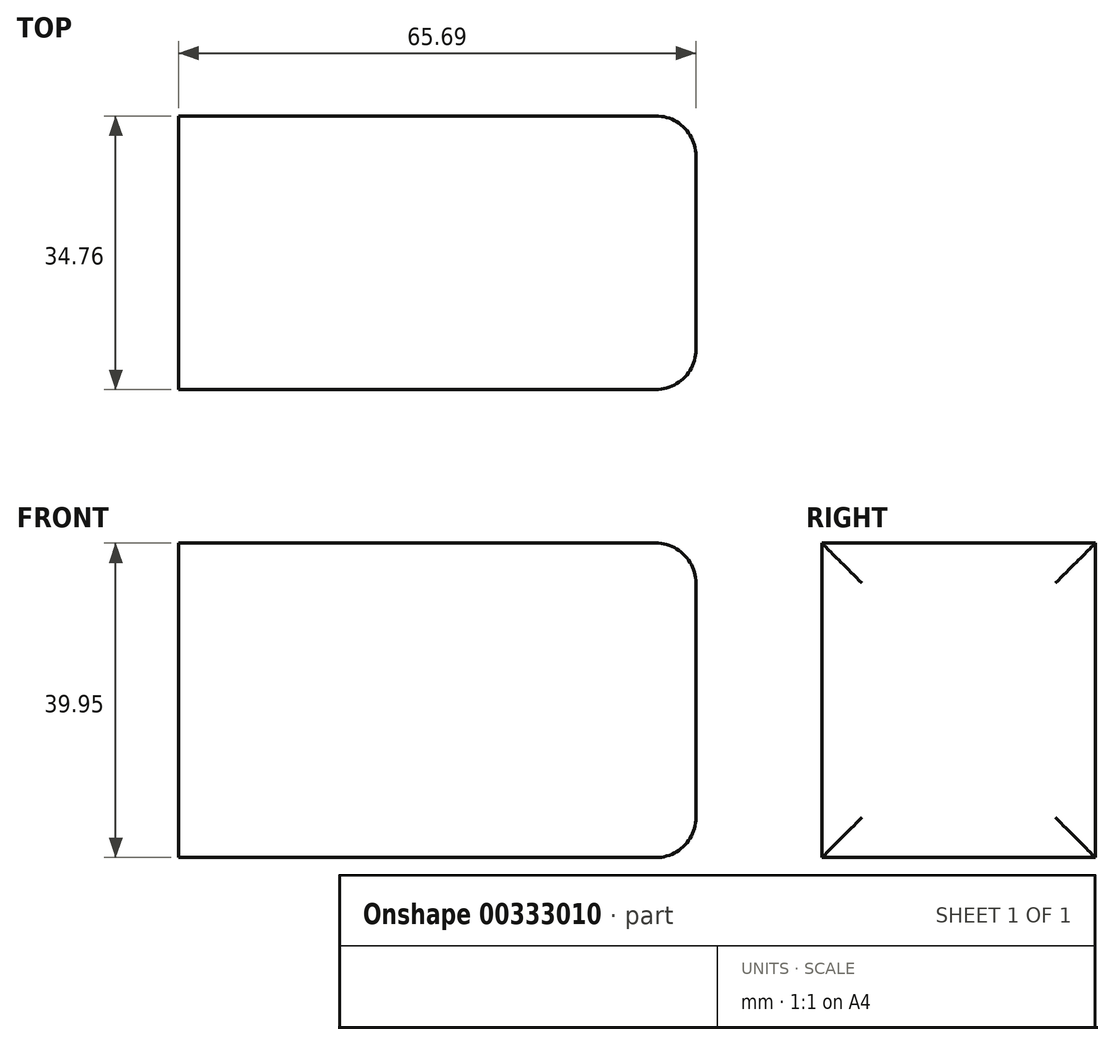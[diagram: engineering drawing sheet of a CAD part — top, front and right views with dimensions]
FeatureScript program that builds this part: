
annotation { "Feature Type Name" : "Feature", "Feature Type Description" : "" }
export const myFeature = defineFeature(function(context is Context, id is Id, definition is map)
    precondition{}
    {
        {
            var Q0;
            Q0=qCreatedBy(makeId("Top.planeOp"),FACE);
            var sketch = newSketch(context, id + "F0", { "sketchPlane" : qUnion([Q0])});
            skLineSegment(sketch, "E0.bottom", {"start": v(35.56, 34.76) * mm, "end": v(-30.13, 34.76) * mm});
            skLineSegment(sketch, "E0.top", {"start": v(35.56, 0) * mm, "end": v(-30.13, 0) * mm});
            skLineSegment(sketch, "E0.left", {"start": v(35.56, 34.76) * mm, "end": v(35.56, 0) * mm});
            skLineSegment(sketch, "E0.right", {"start": v(-30.13, 34.76) * mm, "end": v(-30.13, 0) * mm});
            skLineSegment(sketch, "E1.bottom", {"start": v(0, 19.2) * mm, "end": v(0, 19.2) * mm});
            skLineSegment(sketch, "E1.top", {"start": v(0, 18.72) * mm, "end": v(0, 18.72) * mm});
            skLineSegment(sketch, "E1.left", {"start": v(0, 19.2) * mm, "end": v(0, 18.72) * mm});
            skLineSegment(sketch, "E1.right", {"start": v(0, 19.2) * mm, "end": v(0, 18.72) * mm});
            skSolve(sketch);
        }
        {
            var Q0;
            Q0=makeQuery(id+"F0.imprint","IMPRINT",FACE,{"disambiguationData":[TD([[makeQuery(id+"F0.imprint","IMPRINT",EDGE,{"derivedFrom":sQuery(id+"F0.wireOp",EDGE,"E0.bottom")}),1.0]])]});
            extrude(context, id + "F1", {"entities" : qUnion([Q0]), "depth" : 39.95 * mm});
        }
        {
            var Q0;
            Q0=makeQuery(id+"F1.opExtrude","SWEPT_EDGE",EDGE,{"disambiguationData":[OSD([sQuery(id+"F0.wireOp",EDGE,"E0.bottom"),sQuery(id+"F0.wireOp",EDGE,"E0.left")])]});
            var Q1;
            Q1=makeQuery(id+"F1.opExtrude","CAP_EDGE",EDGE,{"disambiguationData":[OSD([sQuery(id+"F0.wireOp",EDGE,"E0.left")])],"isStart":true});
            var Q2;
            Q2=makeQuery(id+"F1.opExtrude","CAP_EDGE",EDGE,{"disambiguationData":[OSD([sQuery(id+"F0.wireOp",EDGE,"E0.left")])],"isStart":false});
            var Q3;
            Q3=makeQuery(id+"F1.opExtrude","SWEPT_EDGE",EDGE,{"disambiguationData":[OSD([sQuery(id+"F0.wireOp",EDGE,"E0.top"),sQuery(id+"F0.wireOp",EDGE,"E0.left")])]});
            fillet(context, id + "F2", {"entities" : qUnion([Q0, Q1, Q2, Q3]), "radius" : 5.08 * mm, "tangentPropagation" : true, "allowEdgeOverflow" : false});
        }
    });
